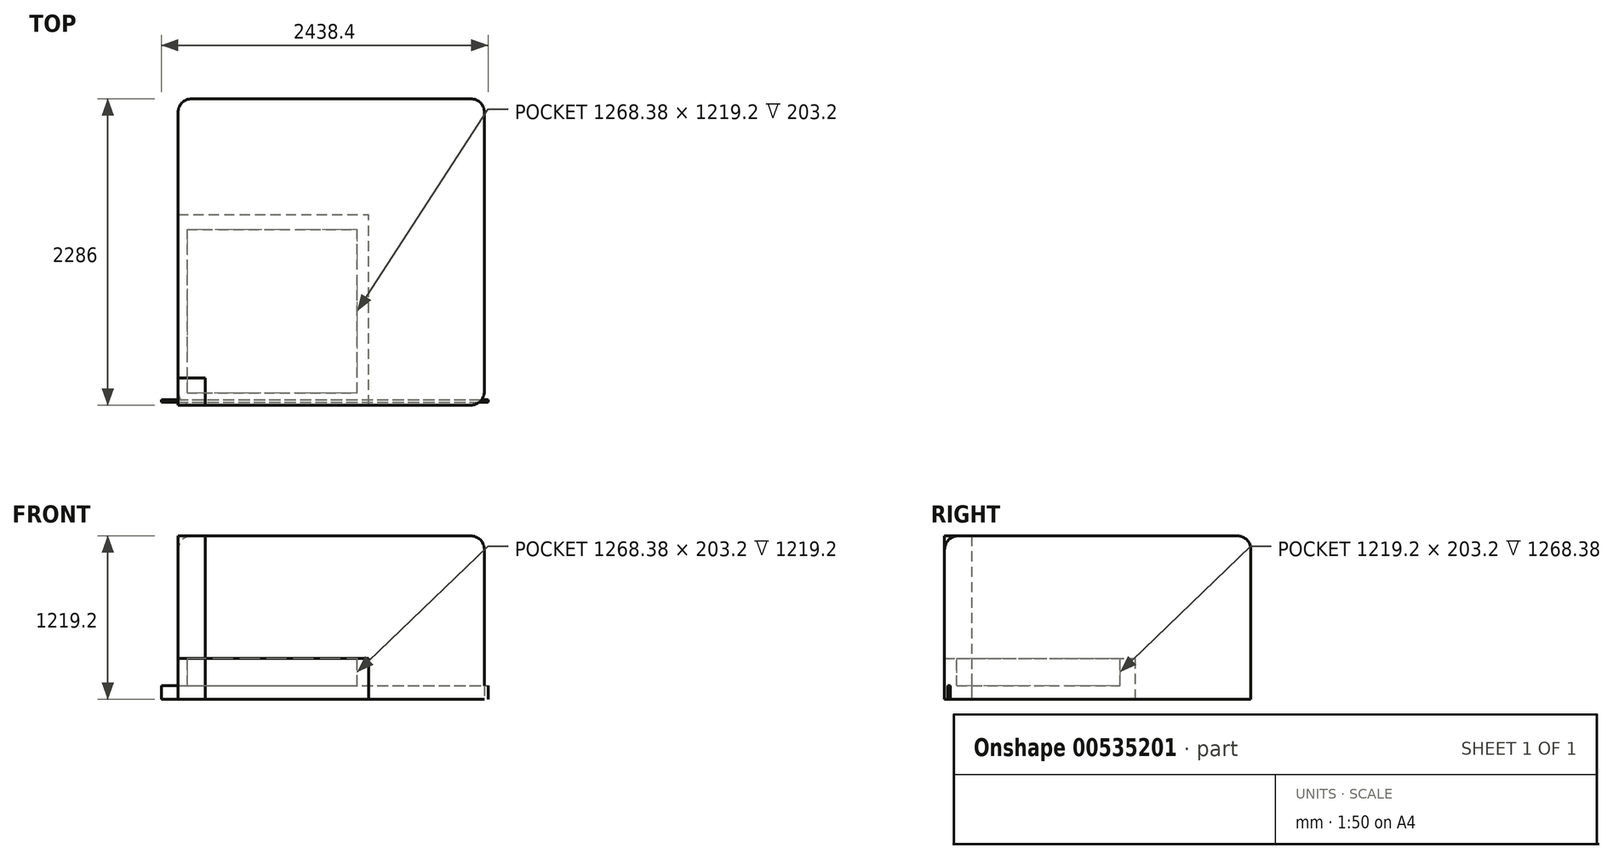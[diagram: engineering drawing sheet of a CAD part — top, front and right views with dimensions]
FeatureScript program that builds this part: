
annotation { "Feature Type Name" : "Feature", "Feature Type Description" : "" }
export const myFeature = defineFeature(function(context is Context, id is Id, definition is map)
    precondition{}
    {
        {
            var Q0;
            Q0=qCreatedBy(makeId("Top.planeOp"),FACE);
            var sketch = newSketch(context, id + "F0", { "sketchPlane" : qUnion([Q0])});
            skLineSegment(sketch, "E0.bottom", {"start": v(-124.83, 42.66) * mm, "end": v(2313.57, 42.66) * mm});
            skLineSegment(sketch, "E0.top", {"start": v(-124.83, 23.6) * mm, "end": v(2313.57, 23.6) * mm});
            skLineSegment(sketch, "E0.left", {"start": v(-124.83, 42.66) * mm, "end": v(-124.83, 23.6) * mm});
            skLineSegment(sketch, "E0.right", {"start": v(2313.57, 42.66) * mm, "end": v(2313.57, 23.6) * mm});
            skSolve(sketch);
        }
        {
            var Q0;
            Q0=makeQuery(id+"F0.imprint","IMPRINT",FACE,{"disambiguationData":[TD([[makeQuery(id+"F0.imprint","IMPRINT",EDGE,{"derivedFrom":sQuery(id+"F0.wireOp",EDGE,"E0.bottom")}),-1.0]])]});
            extrude(context, id + "F1", {"entities" : qUnion([Q0]), "depth" : 101.6 * mm, "offsetDistance" : 25.4 * mm});
        }
        {
            var Q0;
            Q0=qCreatedBy(makeId("Top.planeOp"),FACE);
            var sketch = newSketch(context, id + "F2", { "sketchPlane" : qUnion([Q0])});
            skLineSegment(sketch, "E1.bottom", {"start": v(0, 0) * mm, "end": v(2286, 0) * mm});
            skLineSegment(sketch, "E1.top", {"start": v(0, 2286) * mm, "end": v(2286, 2286) * mm});
            skLineSegment(sketch, "E1.left", {"start": v(0, 0) * mm, "end": v(0, 2286) * mm});
            skLineSegment(sketch, "E1.right", {"start": v(2286, 0) * mm, "end": v(2286, 2286) * mm});
            skSolve(sketch);
        }
        {
            var Q0;
            Q0 = qSketchRegion(id + "F2", true);
            extrude(context, id + "F3", {"entities" : qUnion([Q0]), "depth" : 1219.2 * mm, "offsetDistance" : 25.4 * mm});
        }
        {
            var Q0;
            Q0=makeQuery(id+"F3.opExtrude","CAP_EDGE",EDGE,{"disambiguationData":[OSD([sQuery(id+"F2.wireOp",EDGE,"E1.left")])],"isStart":false});
            var Q1;
            Q1=makeQuery(id+"F3.opExtrude","CAP_EDGE",EDGE,{"disambiguationData":[OSD([sQuery(id+"F2.wireOp",EDGE,"E1.bottom")])],"isStart":false});
            var Q2;
            Q2=makeQuery(id+"F3.opExtrude","CAP_EDGE",EDGE,{"disambiguationData":[OSD([sQuery(id+"F2.wireOp",EDGE,"E1.right")])],"isStart":false});
            var Q3;
            Q3=makeQuery(id+"F3.opExtrude","CAP_EDGE",EDGE,{"disambiguationData":[OSD([sQuery(id+"F2.wireOp",EDGE,"E1.top")])],"isStart":false});
            var Q4;
            Q4=makeQuery(id+"F3.opExtrude","SWEPT_EDGE",EDGE,{"disambiguationData":[OSD([sQuery(id+"F2.wireOp",EDGE,"E1.bottom"),sQuery(id+"F2.wireOp",EDGE,"E1.left")])]});
            var Q5;
            Q5=makeQuery(id+"F3.opExtrude","SWEPT_EDGE",EDGE,{"disambiguationData":[OSD([sQuery(id+"F2.wireOp",EDGE,"E1.bottom"),sQuery(id+"F2.wireOp",EDGE,"E1.right")])]});
            var Q6;
            Q6=makeQuery(id+"F3.opExtrude","SWEPT_EDGE",EDGE,{"disambiguationData":[OSD([sQuery(id+"F2.wireOp",EDGE,"E1.top"),sQuery(id+"F2.wireOp",EDGE,"E1.left")])]});
            var Q7;
            Q7=makeQuery(id+"F3.opExtrude","SWEPT_EDGE",EDGE,{"disambiguationData":[OSD([sQuery(id+"F2.wireOp",EDGE,"E1.top"),sQuery(id+"F2.wireOp",EDGE,"E1.right")])]});
            fillet(context, id + "F4", {"entities" : qUnion([Q0, Q1, Q2, Q3, Q4, Q5, Q6, Q7]), "radius" : 101.6 * mm, "tangentPropagation" : true, "allowEdgeOverflow" : false});
        }
        {
            var Q0;
            Q0=qCreatedBy(makeId("Top.planeOp"),FACE);
            var sketch = newSketch(context, id + "F5", { "sketchPlane" : qUnion([Q0])});
            skLineSegment(sketch, "E2.bottom", {"start": v(0, 0) * mm, "end": v(203.2, 0) * mm});
            skLineSegment(sketch, "E2.top", {"start": v(0, 203.2) * mm, "end": v(203.2, 203.2) * mm});
            skLineSegment(sketch, "E2.left", {"start": v(0, 0) * mm, "end": v(0, 203.2) * mm});
            skLineSegment(sketch, "E2.right", {"start": v(203.2, 0) * mm, "end": v(203.2, 203.2) * mm});
            skSolve(sketch);
        }
        {
            var Q0;
            Q0=makeQuery(id+"F5.imprint","IMPRINT",FACE,{"disambiguationData":[TD([[makeQuery(id+"F5.imprint","IMPRINT",EDGE,{"derivedFrom":sQuery(id+"F5.wireOp",EDGE,"E2.bottom")}),1.0]])]});
            extrude(context, id + "F6", {"entities" : qUnion([Q0]), "depth" : 1219.2 * mm, "offsetDistance" : 25.4 * mm});
        }
        {
            var Q0;
            Q0=qCreatedBy(makeId("Top.planeOp"),FACE);
            var sketch = newSketch(context, id + "F7", { "sketchPlane" : qUnion([Q0])});
            skLineSegment(sketch, "E3.bottom", {"start": v(0, 0) * mm, "end": v(1422.4, 0) * mm});
            skLineSegment(sketch, "E3.top", {"start": v(0, 1422.4) * mm, "end": v(1422.4, 1422.4) * mm});
            skLineSegment(sketch, "E3.left", {"start": v(0, 0) * mm, "end": v(0, 1422.4) * mm});
            skLineSegment(sketch, "E3.right", {"start": v(1422.4, 0) * mm, "end": v(1422.4, 1422.4) * mm});
            skSolve(sketch);
        }
        {
            var Q0;
            Q0 = qSketchRegion(id + "F7", true);
            extrude(context, id + "F8", {"entities" : qUnion([Q0]), "depth" : 304.8 * mm, "offsetDistance" : 25.4 * mm});
        }
        {
            var Q0;
            Q0=makeQuery(id+"F8.opExtrude","CAP_FACE",FACE,{"disambiguationData":[OSD([sQuery(id+"F7.wireOp",EDGE,"E3.bottom"),sQuery(id+"F7.wireOp",EDGE,"E3.top"),sQuery(id+"F7.wireOp",EDGE,"E3.left"),sQuery(id+"F7.wireOp",EDGE,"E3.right")])],"isStart":false});
            var sketch = newSketch(context, id + "F9", { "sketchPlane" : qUnion([Q0])});
            skLineSegment(sketch, "E4.bottom", {"start": v(68.43, 91.84) * mm, "end": v(1336.81, 91.84) * mm});
            skLineSegment(sketch, "E4.top", {"start": v(68.43, 1311.04) * mm, "end": v(1336.81, 1311.04) * mm});
            skLineSegment(sketch, "E4.left", {"start": v(68.43, 91.84) * mm, "end": v(68.43, 1311.04) * mm});
            skLineSegment(sketch, "E4.right", {"start": v(1336.81, 91.84) * mm, "end": v(1336.81, 1311.04) * mm});
            skSolve(sketch);
        }
        {
            var Q0;
            Q0 = qSketchRegion(id + "F9", true);
            extrude(context, id + "F10", {"entities" : qUnion([Q0]), "operationType" : NewBodyOperationType.REMOVE, "oppositeDirection" : true, "depth" : 203.2 * mm, "offsetDistance" : 25.4 * mm});
        }
    });
